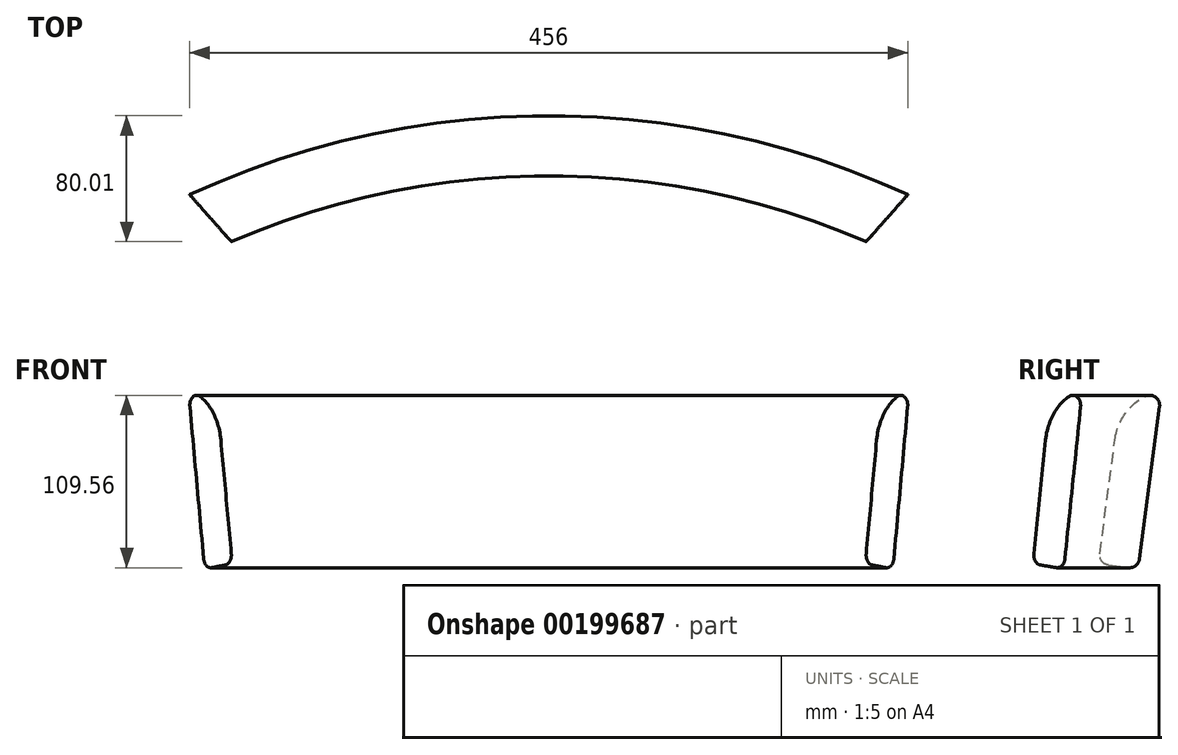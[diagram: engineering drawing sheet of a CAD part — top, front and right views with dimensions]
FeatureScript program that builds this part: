
annotation { "Feature Type Name" : "Feature", "Feature Type Description" : "" }
export const myFeature = defineFeature(function(context is Context, id is Id, definition is map)
    precondition{}
    {
        {
            var Q0;
            Q0=qCreatedBy(makeId("Top.planeOp"),FACE);
            var sketch = newSketch(context, id + "F0", { "sketchPlane" : qUnion([Q0])});
            skLineSegment(sketch, "E0", {"start": v(0, 295.34) * mm, "end": v(0, -384.42) * mm, "construction": true});
            skCircle(sketch, "E1", {"center": v(0, -296.5) * mm, "radius": 444.5 * mm});
            skSolve(sketch);
        }
        {
            var Q0;
            Q0=qCreatedBy(makeId("Right.planeOp"),FACE);
            var sketch = newSketch(context, id + "F1", { "sketchPlane" : qUnion([Q0])});
            skLineSegment(sketch, "E2", {"start": v(248.05, 104.87) * mm, "end": v(248.05, -136.27) * mm, "construction": true});
            skLineSegment(sketch, "E3", {"start": v(246.72, 21.21) * mm, "end": v(233.96, -75.65) * mm});
            skLineSegment(sketch, "E4", {"start": v(226.84, -81.12) * mm, "end": v(214.25, -79.46) * mm});
            skLineSegment(sketch, "E5", {"start": v(208.78, -72.34) * mm, "end": v(218.3, 0) * mm});
            skArc(sketch, "E6", {"start": v(237.42, 27.64) * mm, "mid": v(224.52, 16.13) * mm, "end": v(218.3, 0) * mm});
            skPoint(sketch, "E7.visualSharp", {"position": v(207.95, -78.63) * mm});
            skArc(sketch, "E7.filletArc", {"start": v(208.78, -72.34) * mm, "mid": v(210.04, -77.03) * mm, "end": v(214.25, -79.46) * mm});
            skPoint(sketch, "E8.visualSharp", {"position": v(233.13, -81.95) * mm});
            skArc(sketch, "E8.filletArc", {"start": v(226.84, -81.12) * mm, "mid": v(231.53, -79.86) * mm, "end": v(233.96, -75.65) * mm});
            skPoint(sketch, "E9.visualSharp", {"position": v(248.05, 31.38) * mm});
            skArc(sketch, "E9.filletArc", {"start": v(246.72, 21.21) * mm, "mid": v(244.03, 27.27) * mm, "end": v(237.42, 27.64) * mm});
            skSolve(sketch);
        }
        {
            var Q0;
            Q0=makeQuery(id+"F1.imprint","IMPRINT",FACE,{"disambiguationData":[TD([[makeQuery(id+"F1.imprint","IMPRINT",EDGE,{"derivedFrom":sQuery(id+"F1.wireOp",EDGE,"E3")}),-1.0]])]});
            var Q1;
            Q1=sQuery(id+"F0.wireOp",EDGE,"E1");
            revolve(context, id + "F2", {"entities" : qUnion([Q0]), "axis" : qUnion([Q1]), "revolveType" : RevolveType.SYMMETRIC, "angle" : 60 * degree});
        }
        {
            var Q0;
            Q0=qCreatedBy(makeId("Top.planeOp"),FACE);
            cPlane(context, id + "F3", {"entities" : qUnion([Q0]), "cplaneType" : CPlaneType.OFFSET, "offset" : 50.8 * mm, "width" : 152.4 * mm, "height" : 152.4 * mm});
        }
        {
            var Q0;
            Q0=qCreatedBy(id+"F3.planeOp",FACE);
            var sketch = newSketch(context, id + "F4", { "sketchPlane" : qUnion([Q0])});
            skLineSegment(sketch, "E10", {"start": v(0, 344.4) * mm, "end": v(0, -61.1) * mm, "construction": true});
            skLineSegment(sketch, "E11", {"start": v(0, -61.1) * mm, "end": v(-264.1, 237.4) * mm});
            skPoint(sketch, "E12", {"position": v(0, 218.3) * mm});
            skLineSegment(sketch, "E13", {"start": v(0, -61.1) * mm, "end": v(259.9, 232.67) * mm});
            skLineSegment(sketch, "E14", {"start": v(-264.1, 237.4) * mm, "end": v(-321.9, 178.6) * mm});
            skLineSegment(sketch, "E15", {"start": v(-321.9, 178.6) * mm, "end": v(-55.83, -112.62) * mm});
            skLineSegment(sketch, "E16", {"start": v(-55.83, -112.62) * mm, "end": v(1.92, -175.83) * mm});
            skLineSegment(sketch, "E17", {"start": v(1.92, -175.83) * mm, "end": v(398.38, 212) * mm});
            skLineSegment(sketch, "E18", {"start": v(398.38, 212) * mm, "end": v(259.9, 232.67) * mm});
            skSolve(sketch);
        }
        {
            var Q0;
            Q0=makeQuery(id+"F4.imprint","IMPRINT",FACE,{"disambiguationData":[TD([[makeQuery(id+"F4.imprint","IMPRINT",EDGE,{"derivedFrom":sQuery(id+"F4.wireOp",EDGE,"E11")}),1.0]])]});
            extrude(context, id + "F5", {"entities" : qUnion([Q0]), "operationType" : NewBodyOperationType.REMOVE, "endBound" : BoundingType.THROUGH_ALL, "oppositeDirection" : true, "depth" : 25.4 * mm});
        }
    });
